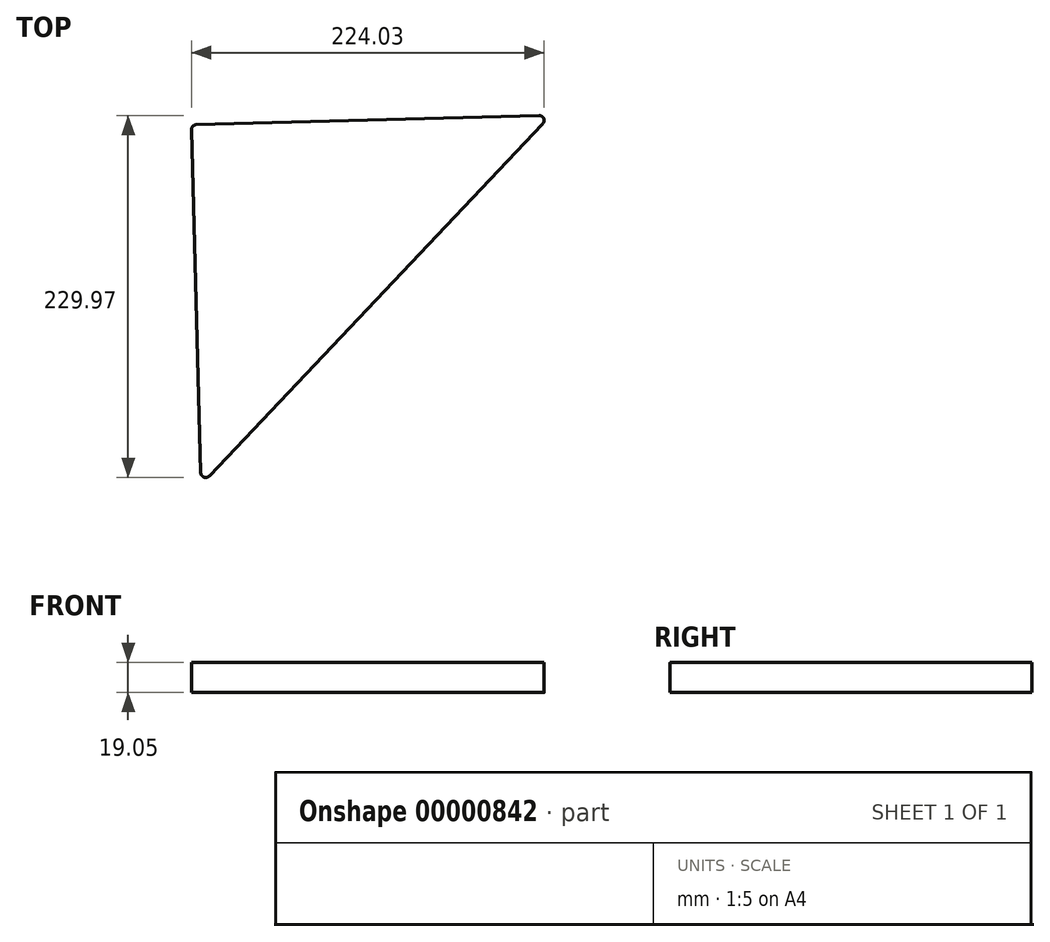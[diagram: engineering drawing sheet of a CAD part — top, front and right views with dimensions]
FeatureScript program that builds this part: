
annotation { "Feature Type Name" : "Feature", "Feature Type Description" : "" }
export const myFeature = defineFeature(function(context is Context, id is Id, definition is map)
    precondition{}
    {
        {
            var Q0;
            Q0=qCreatedBy(makeId("Top.planeOp"),FACE);
            var sketch = newSketch(context, id + "F0", { "sketchPlane" : qUnion([Q0])});
            skLineSegment(sketch, "E0.bottom", {"start": v(-111.35, -109.71) * mm, "end": v(-117.29, 107.96) * mm});
            skLineSegment(sketch, "E0.right", {"start": v(-114.2, 111.22) * mm, "end": v(103.48, 117.17) * mm});
            skLineSegment(sketch, "E1", {"start": v(-105.87, -111.81) * mm, "end": v(105.87, 111.81) * mm});
            skPoint(sketch, "E2.visualSharp", {"position": v(-117.38, 111.14) * mm});
            skArc(sketch, "E2.filletArc", {"start": v(-114.2, 111.22) * mm, "mid": v(-116.42, 110.23) * mm, "end": v(-117.29, 107.96) * mm});
            skPoint(sketch, "E3.visualSharp", {"position": v(111.14, 117.38) * mm});
            skArc(sketch, "E3.filletArc", {"start": v(105.87, 111.81) * mm, "mid": v(106.46, 115.29) * mm, "end": v(103.48, 117.17) * mm});
            skPoint(sketch, "E4.visualSharp", {"position": v(-111.14, -117.38) * mm});
            skArc(sketch, "E4.filletArc", {"start": v(-111.35, -109.71) * mm, "mid": v(-109.3, -112.6) * mm, "end": v(-105.87, -111.81) * mm});
            skSolve(sketch);
        }
        {
            var Q0;
            Q0 = qSketchRegion(id + "F0", true);
            extrude(context, id + "F1", {"entities" : qUnion([Q0]), "oppositeDirection" : true, "depth" : 19.05 * mm});
        }
    });
